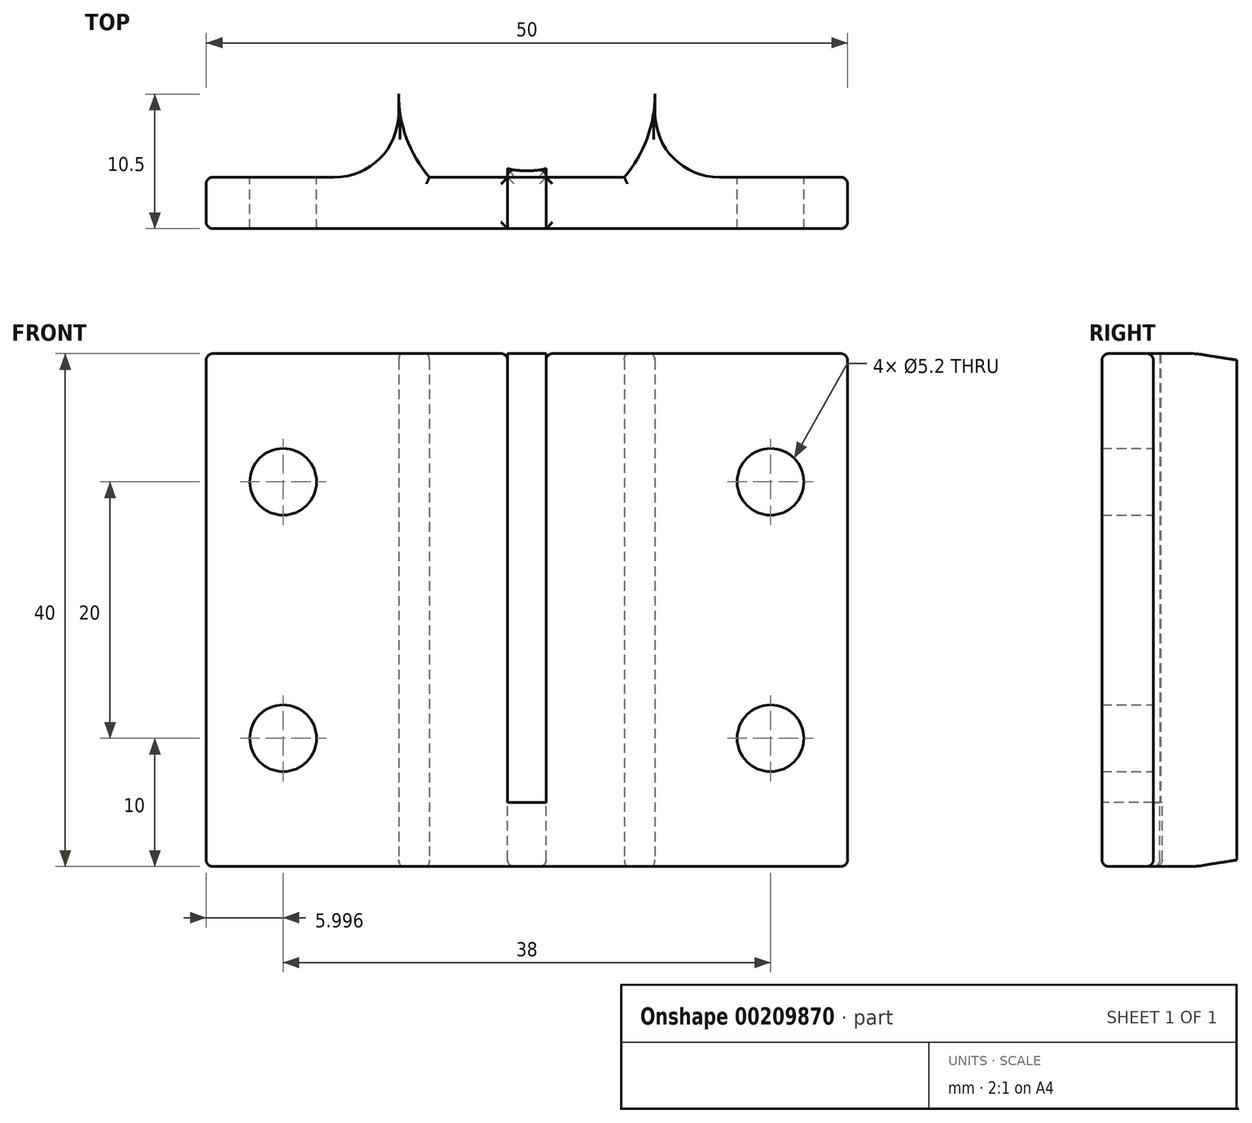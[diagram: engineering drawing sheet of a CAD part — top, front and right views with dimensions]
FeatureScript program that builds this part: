
annotation { "Feature Type Name" : "Feature", "Feature Type Description" : "" }
export const myFeature = defineFeature(function(context is Context, id is Id, definition is map)
    precondition{}
    {
        {
            var Q0;
            Q0=qCreatedBy(makeId("Top.planeOp"),FACE);
            var sketch = newSketch(context, id + "F0", { "sketchPlane" : qUnion([Q0])});
            skCircle(sketch, "E0", {"center": v(-24.33, 35.38) * mm, "radius": 6 * mm});
            skCircle(sketch, "E1", {"center": v(-24.33, 35.38) * mm, "radius": 10 * mm});
            skLineSegment(sketch, "E2", {"start": v(-24.33, 35.38) * mm, "end": v(-24.33, 24.88) * mm, "construction": true});
            skLineSegment(sketch, "E3.bottom", {"start": v(-49.33, 24.88) * mm, "end": v(0.67, 24.88) * mm});
            skLineSegment(sketch, "E3.top", {"start": v(-49.33, 28.88) * mm, "end": v(0.67, 28.88) * mm});
            skLineSegment(sketch, "E3.left", {"start": v(-49.33, 24.88) * mm, "end": v(-49.33, 28.88) * mm});
            skLineSegment(sketch, "E3.right", {"start": v(0.67, 24.88) * mm, "end": v(0.67, 28.88) * mm});
            skLineSegment(sketch, "E4", {"start": v(-34.33, 35.38) * mm, "end": v(-14.33, 35.38) * mm, "construction": true});
            skLineSegment(sketch, "E5", {"start": v(-34.33, 35.38) * mm, "end": v(-34.33, 28.88) * mm});
            skLineSegment(sketch, "E6", {"start": v(-14.33, 35.38) * mm, "end": v(-14.33, 28.88) * mm});
            skLineSegment(sketch, "E7", {"start": v(-25.83, 29.57) * mm, "end": v(-25.83, 24.88) * mm});
            skLineSegment(sketch, "E8", {"start": v(-22.83, 29.57) * mm, "end": v(-22.83, 24.88) * mm});
            skSolve(sketch);
        }
        {
            var Q0;
            {var subQ0=sQuery(id+"F0.wireOp",EDGE,"E3.top");var subQ1=sQuery(id+"F0.wireOp",EDGE,"E1");var subQ2=makeQuery(id+"F0.imprint","INTERSECT",VERTEX,{"disambiguationData":[OD(0.0)],"derivedFrom":[subQ1,subQ0]});Q0=makeQuery(id+"F0.imprint","IMPRINT",FACE,{"disambiguationData":[TD([[makeQuery(id+"F0.imprint","IMPRINT",EDGE,{"disambiguationData":[TD([[subQ2,-1.0]])],"derivedFrom":subQ1}),1.0]])]});}
            var Q1;
            {var subQ3=sQuery(id+"F0.wireOp",EDGE,"E5");Q1=makeQuery(id+"F0.imprint","IMPRINT",FACE,{"disambiguationData":[TD([[makeQuery(id+"F0.imprint","IMPRINT",EDGE,{"derivedFrom":subQ3}),1.0]])]});}
            var Q2;
            {var subQ0=sQuery(id+"F0.wireOp",EDGE,"E6");Q2=makeQuery(id+"F0.imprint","IMPRINT",FACE,{"disambiguationData":[TD([[makeQuery(id+"F0.imprint","IMPRINT",EDGE,{"derivedFrom":subQ0}),-1.0]])]});}
            var Q3;
            Q3=makeQuery(id+"F0.imprint","IMPRINT",FACE,{"disambiguationData":[TD([[makeQuery(id+"F0.imprint","IMPRINT",EDGE,{"derivedFrom":sQuery(id+"F0.wireOp",EDGE,"E0")}),-1.0]])]});
            var Q4;
            {var subQ0=sQuery(id+"F0.wireOp",EDGE,"E8");var subQ1=sQuery(id+"F0.wireOp",EDGE,"E1");var subQ2=makeQuery(id+"F0.imprint","INTERSECT",VERTEX,{"derivedFrom":[subQ1,subQ0]});Q4=makeQuery(id+"F0.imprint","IMPRINT",FACE,{"disambiguationData":[TD([[makeQuery(id+"F0.imprint","IMPRINT",EDGE,{"disambiguationData":[TD([[subQ2,-1.0]])],"derivedFrom":subQ1}),1.0]])]});}
            var Q5;
            {var subQ3=sQuery(id+"F0.wireOp",EDGE,"E3.right");Q5=makeQuery(id+"F0.imprint","IMPRINT",FACE,{"disambiguationData":[TD([[makeQuery(id+"F0.imprint","IMPRINT",EDGE,{"derivedFrom":subQ3}),1.0]])]});}
            var Q6;
            {var subQ4=sQuery(id+"F0.wireOp",EDGE,"E3.left");Q6=makeQuery(id+"F0.imprint","IMPRINT",FACE,{"disambiguationData":[TD([[makeQuery(id+"F0.imprint","IMPRINT",EDGE,{"derivedFrom":subQ4}),-1.0]])]});}
            extrude(context, id + "F1", {"entities" : qUnion([Q0, Q1, Q2, Q3, Q4, Q5, Q6]), "depth" : 35 * mm, "offsetDistance" : 25 * mm});
        }
        {
            var Q0;
            {var subQ4=sQuery(id+"F0.wireOp",EDGE,"E3.left");Q0=makeQuery(id+"F0.imprint","IMPRINT",FACE,{"disambiguationData":[TD([[makeQuery(id+"F0.imprint","IMPRINT",EDGE,{"derivedFrom":subQ4}),-1.0]])]});}
            var Q1;
            {var subQ3=sQuery(id+"F0.wireOp",EDGE,"E5");Q1=makeQuery(id+"F0.imprint","IMPRINT",FACE,{"disambiguationData":[TD([[makeQuery(id+"F0.imprint","IMPRINT",EDGE,{"derivedFrom":subQ3}),1.0]])]});}
            var Q2;
            {var subQ10=sQuery(id+"F0.wireOp",EDGE,"E0");var subQ11=makeQuery(id+"F0.imprint","IMPRINT",VERTEX,{"derivedFrom":subQ10});Q2=makeQuery(id+"F0.imprint","IMPRINT",FACE,{"disambiguationData":[TD([[makeQuery(id+"F0.imprint","IMPRINT",EDGE,{"disambiguationData":[TD([[subQ11,1.0]])],"derivedFrom":subQ10}),-1.0]])]});}
            var Q3;
            {var subQ0=sQuery(id+"F0.wireOp",EDGE,"E0");var subQ3=makeQuery(id+"F0.imprint","IMPRINT",VERTEX,{"derivedFrom":subQ0});Q3=makeQuery(id+"F0.imprint","IMPRINT",FACE,{"disambiguationData":[TD([[makeQuery(id+"F0.imprint","IMPRINT",EDGE,{"disambiguationData":[TD([[subQ3,1.0]])],"derivedFrom":subQ0}),1.0]])]});}
            var Q4;
            {var subQ0=sQuery(id+"F0.wireOp",EDGE,"E8");var subQ1=sQuery(id+"F0.wireOp",EDGE,"E1");var subQ2=makeQuery(id+"F0.imprint","INTERSECT",VERTEX,{"derivedFrom":[subQ1,subQ0]});Q4=makeQuery(id+"F0.imprint","IMPRINT",FACE,{"disambiguationData":[TD([[makeQuery(id+"F0.imprint","IMPRINT",EDGE,{"disambiguationData":[TD([[subQ2,-1.0]])],"derivedFrom":subQ1}),1.0]])]});}
            var Q5;
            {var subQ0=sQuery(id+"F0.wireOp",EDGE,"E6");Q5=makeQuery(id+"F0.imprint","IMPRINT",FACE,{"disambiguationData":[TD([[makeQuery(id+"F0.imprint","IMPRINT",EDGE,{"derivedFrom":subQ0}),-1.0]])]});}
            var Q6;
            {var subQ0=sQuery(id+"F0.wireOp",EDGE,"E3.top");var subQ1=sQuery(id+"F0.wireOp",EDGE,"E1");var subQ2=makeQuery(id+"F0.imprint","INTERSECT",VERTEX,{"disambiguationData":[OD(0.0)],"derivedFrom":[subQ1,subQ0]});Q6=makeQuery(id+"F0.imprint","IMPRINT",FACE,{"disambiguationData":[TD([[makeQuery(id+"F0.imprint","IMPRINT",EDGE,{"disambiguationData":[TD([[subQ2,-1.0]])],"derivedFrom":subQ1}),1.0]])]});}
            var Q7;
            {var subQ0=sQuery(id+"F0.wireOp",EDGE,"E3.right");Q7=makeQuery(id+"F0.imprint","IMPRINT",FACE,{"disambiguationData":[TD([[makeQuery(id+"F0.imprint","IMPRINT",EDGE,{"derivedFrom":subQ0}),1.0]])]});}
            var Q8;
            {var subQ0=sQuery(id+"F0.wireOp",EDGE,"E7");var subQ1=sQuery(id+"F0.wireOp",EDGE,"E1");var subQ2=makeQuery(id+"F0.imprint","INTERSECT",VERTEX,{"derivedFrom":[subQ1,subQ0]});Q8=makeQuery(id+"F0.imprint","IMPRINT",FACE,{"disambiguationData":[TD([[makeQuery(id+"F0.imprint","IMPRINT",EDGE,{"disambiguationData":[TD([[subQ2,-1.0]])],"derivedFrom":subQ1}),1.0]])]});}
            var Q9;
            {var subQ0=sQuery(id+"F0.wireOp",EDGE,"E8");var subQ1=sQuery(id+"F0.wireOp",EDGE,"E0");var subQ2=makeQuery(id+"F0.imprint","INTERSECT",VERTEX,{"derivedFrom":[subQ1,subQ0]});Q9=makeQuery(id+"F0.imprint","IMPRINT",FACE,{"disambiguationData":[TD([[makeQuery(id+"F0.imprint","IMPRINT",EDGE,{"disambiguationData":[TD([[subQ2,1.0]])],"derivedFrom":subQ1}),-1.0]])]});}
            var Q10;
            {var subQ0=sQuery(id+"F0.wireOp",EDGE,"E7");var subQ1=sQuery(id+"F0.wireOp",EDGE,"E1");var subQ2=makeQuery(id+"F0.imprint","INTERSECT",VERTEX,{"derivedFrom":[subQ1,subQ0]});Q10=makeQuery(id+"F0.imprint","IMPRINT",FACE,{"disambiguationData":[TD([[makeQuery(id+"F0.imprint","IMPRINT",EDGE,{"disambiguationData":[TD([[subQ2,-1.0]])],"derivedFrom":subQ1}),-1.0]])]});}
            extrude(context, id + "F2", {"entities" : qUnion([Q0, Q1, Q2, Q3, Q4, Q5, Q6, Q7, Q8, Q9, Q10]), "oppositeDirection" : true, "depth" : 5 * mm, "offsetDistance" : 25 * mm});
        }
        {
            var Q0;
            Q0=makeQuery(id+"F1.opExtrude","SWEPT_BODY",BODY,{"disambiguationData":[OSD([sQuery(id+"F0.wireOp",EDGE,"E0"),sQuery(id+"F0.wireOp",EDGE,"E1"),sQuery(id+"F0.wireOp",EDGE,"E3.bottom"),sQuery(id+"F0.wireOp",EDGE,"E3.top"),sQuery(id+"F0.wireOp",EDGE,"E3.left"),sQuery(id+"F0.wireOp",EDGE,"E3.right"),sQuery(id+"F0.wireOp",EDGE,"E5"),sQuery(id+"F0.wireOp",EDGE,"E6"),sQuery(id+"F0.wireOp",EDGE,"E7"),sQuery(id+"F0.wireOp",EDGE,"E8")])]});
            var Q1;
            Q1=makeQuery(id+"F2.opExtrude","SWEPT_BODY",BODY,{"disambiguationData":[OSD([sQuery(id+"F0.wireOp",EDGE,"E1"),sQuery(id+"F0.wireOp",EDGE,"E3.bottom"),sQuery(id+"F0.wireOp",EDGE,"E3.top"),sQuery(id+"F0.wireOp",EDGE,"E3.left"),sQuery(id+"F0.wireOp",EDGE,"E3.right"),sQuery(id+"F0.wireOp",EDGE,"E5"),sQuery(id+"F0.wireOp",EDGE,"E6")])]});
            booleanBodies(context, id + "F3", {"operationType" : BooleanOperationType.UNION, "tools" : qUnion([Q0, Q1])});
        }
        {
            var Q0;
            Q0=makeQuery(id+"F1.opExtrude","SWEPT_EDGE",EDGE,{"disambiguationData":[OSD([sQuery(id+"F0.wireOp",EDGE,"E3.top"),sQuery(id+"F0.wireOp",EDGE,"E5")])]});
            var Q1;
            Q1=makeQuery(id+"F1.opExtrude","SWEPT_EDGE",EDGE,{"disambiguationData":[OSD([sQuery(id+"F0.wireOp",EDGE,"E3.top"),sQuery(id+"F0.wireOp",EDGE,"E6")])]});
            fillet(context, id + "F4", {"entities" : qUnion([Q0, Q1]), "tangentPropagation" : true, "radius" : 5 * mm, "defaultsChanged" : true, "vertexSettings" : [], "allowEdgeOverflow" : false});
        }
        {
            var Q0;
            {var subQ0=sQuery(id+"F0.wireOp",EDGE,"E3.top");Q0=makeQuery(id+"F1.opExtrude","SWEPT_FACE",FACE,{"disambiguationData":[OSD([subQ0]),TDD([makeQuery(id+"F0.imprint","IMPRINT",EDGE,{"disambiguationData":[TD([[makeQuery(id+"F0.imprint","INTERSECT",VERTEX,{"derivedFrom":[subQ0,sQuery(id+"F0.wireOp",EDGE,"E3.right")]}),1.0]])],"derivedFrom":subQ0})])]});}
            var sketch = newSketch(context, id + "F5", { "sketchPlane" : qUnion([Q0])});
            skPoint(sketch, "E9", {"position": v(5.33, 25) * mm});
            skPoint(sketch, "E10", {"position": v(5.33, 5) * mm});
            skPoint(sketch, "E11", {"position": v(43.33, 25) * mm});
            skPoint(sketch, "E12", {"position": v(43.33, 5) * mm});
            skSolve(sketch);
        }
        {
            var Q0;
            Q0=sQuery(id+"F5.wireOp",VERTEX,"E9");
            var Q1;
            Q1=sQuery(id+"F5.wireOp",VERTEX,"E10");
            var Q2;
            Q2=sQuery(id+"F5.wireOp",VERTEX,"E11");
            var Q3;
            Q3=sQuery(id+"F5.wireOp",VERTEX,"E12");
            var Q4;
            Q4=makeQuery(id+"F1.opExtrude","SWEPT_BODY",BODY,{"disambiguationData":[OSD([sQuery(id+"F0.wireOp",EDGE,"E0"),sQuery(id+"F0.wireOp",EDGE,"E1"),sQuery(id+"F0.wireOp",EDGE,"E3.bottom"),sQuery(id+"F0.wireOp",EDGE,"E3.top"),sQuery(id+"F0.wireOp",EDGE,"E3.left"),sQuery(id+"F0.wireOp",EDGE,"E3.right"),sQuery(id+"F0.wireOp",EDGE,"E5"),sQuery(id+"F0.wireOp",EDGE,"E6"),sQuery(id+"F0.wireOp",EDGE,"E7"),sQuery(id+"F0.wireOp",EDGE,"E8")])]});
            hole(context, id + "F6", {"style" : HoleStyle.SIMPLE, "endStyle" : HoleEndStyle.BLIND, "holeDiameter" : 5.2 * mm, "majorDiameter" : 5 * mm, "holeDepth" : 10 * mm, "isTappedThrough" : true, "tappedDepth" : 12 * mm, "tapClearance" : 3, "locations" : qUnion([Q0, Q1, Q2, Q3]), "scope" : qUnion([Q4])});
        }
        {
            var Q0;
            Q0=makeQuery(id+"F2.opExtrude","CAP_FACE",FACE,{"disambiguationData":[OSD([sQuery(id+"F0.wireOp",EDGE,"E1"),sQuery(id+"F0.wireOp",EDGE,"E3.bottom"),sQuery(id+"F0.wireOp",EDGE,"E3.top"),sQuery(id+"F0.wireOp",EDGE,"E3.left"),sQuery(id+"F0.wireOp",EDGE,"E3.right"),sQuery(id+"F0.wireOp",EDGE,"E5"),sQuery(id+"F0.wireOp",EDGE,"E6")])],"isStart":false});
            var Q1;
            Q1=makeQuery(id+"F1.opExtrude","CAP_FACE",FACE,{"disambiguationData":[OSD([sQuery(id+"F0.wireOp",EDGE,"E0"),sQuery(id+"F0.wireOp",EDGE,"E1"),sQuery(id+"F0.wireOp",EDGE,"E3.bottom"),sQuery(id+"F0.wireOp",EDGE,"E3.top"),sQuery(id+"F0.wireOp",EDGE,"E3.left"),sQuery(id+"F0.wireOp",EDGE,"E3.right"),sQuery(id+"F0.wireOp",EDGE,"E5"),sQuery(id+"F0.wireOp",EDGE,"E6"),sQuery(id+"F0.wireOp",EDGE,"E7"),sQuery(id+"F0.wireOp",EDGE,"E8")])],"isStart":false});
            var Q2;
            {var subQ0=sQuery(id+"F0.wireOp",EDGE,"E3.left");Q2=makeQuery(id+"F3.opBoolean","MERGE",FACE,{"derivedFrom":[makeQuery(id+"F1.opExtrude","SWEPT_FACE",FACE,{"disambiguationData":[OSD([subQ0])]}),makeQuery(id+"F2.opExtrude","SWEPT_FACE",FACE,{"disambiguationData":[OSD([subQ0])]})]});}
            var Q3;
            {var subQ0=sQuery(id+"F0.wireOp",EDGE,"E3.right");Q3=makeQuery(id+"F3.opBoolean","MERGE",FACE,{"derivedFrom":[makeQuery(id+"F1.opExtrude","SWEPT_FACE",FACE,{"disambiguationData":[OSD([subQ0])]}),makeQuery(id+"F2.opExtrude","SWEPT_FACE",FACE,{"disambiguationData":[OSD([subQ0])]})]});}
            var Q4;
            Q4=makeQuery(id+"F1.opExtrude","SWEPT_EDGE",EDGE,{"disambiguationData":[OSD([sQuery(id+"F0.wireOp",EDGE,"E0"),sQuery(id+"F0.wireOp",EDGE,"E7")])]});
            var Q5;
            Q5=makeQuery(id+"F1.opExtrude","SWEPT_EDGE",EDGE,{"disambiguationData":[OSD([sQuery(id+"F0.wireOp",EDGE,"E0"),sQuery(id+"F0.wireOp",EDGE,"E8")])]});
            fillet(context, id + "F7", {"entities" : qUnion([Q0, Q1, Q2, Q3, Q4, Q5]), "tangentPropagation" : true, "radius" : 0.5 * mm, "defaultsChanged" : false, "vertexSettings" : [], "allowEdgeOverflow" : false});
        }
    });
